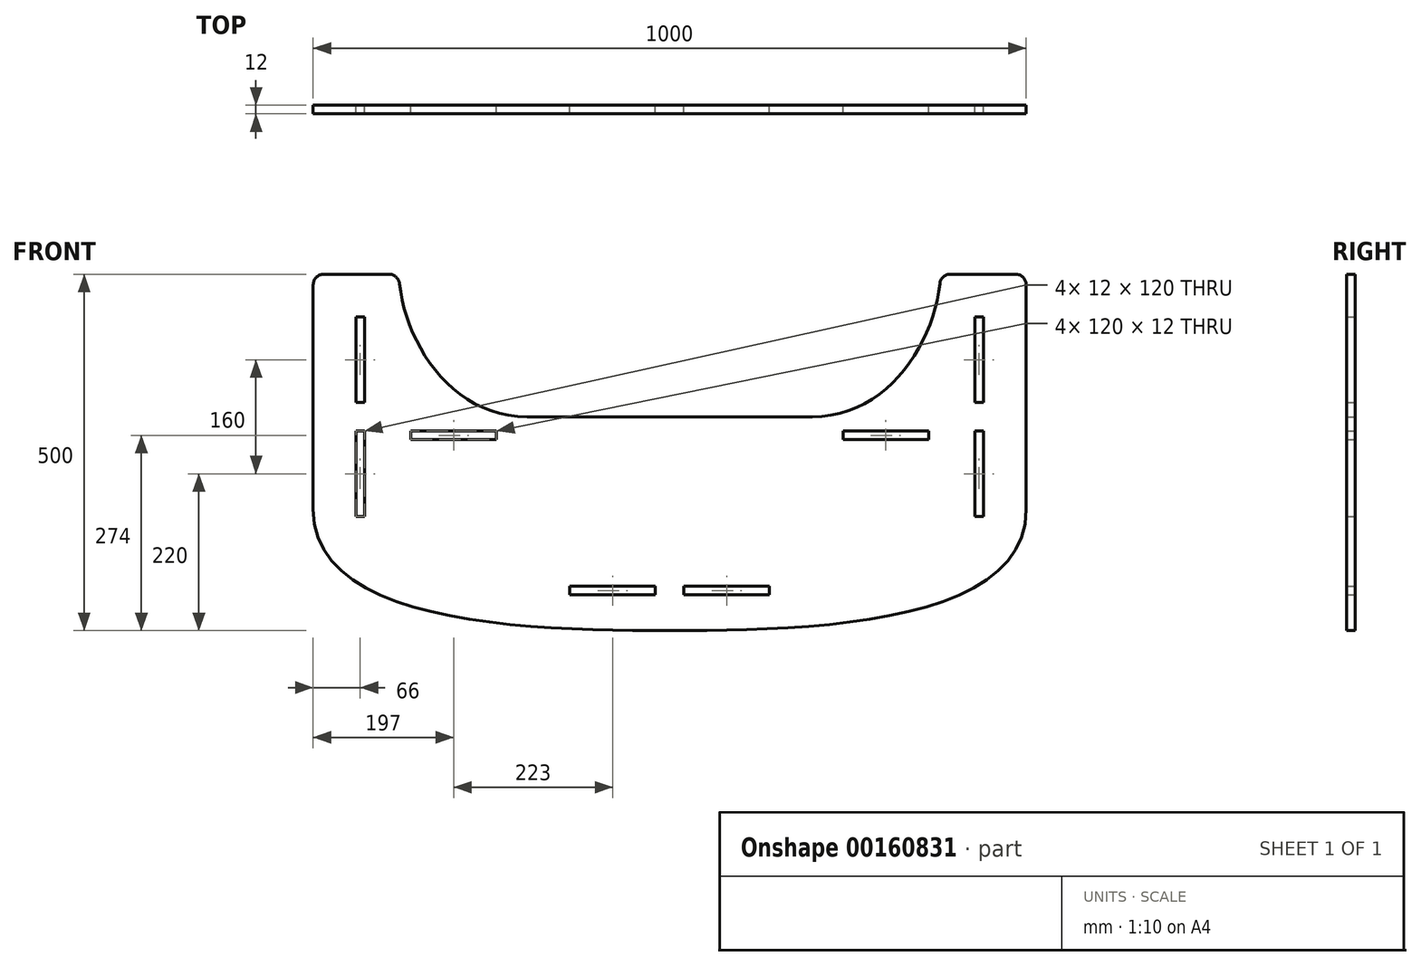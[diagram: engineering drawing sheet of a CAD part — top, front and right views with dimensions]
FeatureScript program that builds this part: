
annotation { "Feature Type Name" : "Feature", "Feature Type Description" : "" }
export const myFeature = defineFeature(function(context is Context, id is Id, definition is map)
    precondition{}
    {
        {
            var Q0;
            Q0=qCreatedBy(makeId("Front.planeOp"),FACE);
            var sketch = newSketch(context, id + "F0", { "sketchPlane" : qUnion([Q0])});
            skLineSegment(sketch, "E0", {"start": v(0, 0) * mm, "end": v(0, 300) * mm, "construction": true});
            skLineSegment(sketch, "E1", {"start": v(-393.84, 500) * mm, "end": v(-485, 500) * mm});
            skLineSegment(sketch, "E2", {"start": v(-500, 485) * mm, "end": v(-500, 170) * mm});
            skFitSpline(sketch, "E3", {"points": [v(-500, 170) * mm, v(0, 0) * mm], "startDerivative": vector(0, -492.34) * mm, "endDerivative": vector(572.83, 0) * mm});
            skLineSegment(sketch, "E4", {"start": v(-440, 440) * mm, "end": v(-440, 320) * mm});
            skLineSegment(sketch, "E5", {"start": v(-428, 320) * mm, "end": v(-428, 440) * mm});
            skLineSegment(sketch, "E6", {"start": v(-428, 440) * mm, "end": v(-440, 440) * mm});
            skLineSegment(sketch, "E7.bottom", {"start": v(-440, 280) * mm, "end": v(-428, 280) * mm});
            skLineSegment(sketch, "E7.top", {"start": v(-440, 160) * mm, "end": v(-428, 160) * mm});
            skLineSegment(sketch, "E7.left", {"start": v(-440, 280) * mm, "end": v(-440, 160) * mm});
            skLineSegment(sketch, "E7.right", {"start": v(-428, 280) * mm, "end": v(-428, 160) * mm});
            skLineSegment(sketch, "E8.bottom", {"start": v(-363, 280) * mm, "end": v(-243, 280) * mm});
            skLineSegment(sketch, "E8.top", {"start": v(-363, 268) * mm, "end": v(-243, 268) * mm});
            skLineSegment(sketch, "E8.left", {"start": v(-363, 280) * mm, "end": v(-363, 268) * mm});
            skLineSegment(sketch, "E8.right", {"start": v(-243, 280) * mm, "end": v(-243, 268) * mm});
            skLineSegment(sketch, "E9.bottom", {"start": v(-140, 62) * mm, "end": v(-20, 62) * mm});
            skLineSegment(sketch, "E9.top", {"start": v(-140, 50) * mm, "end": v(-20, 50) * mm});
            skLineSegment(sketch, "E9.left", {"start": v(-140, 62) * mm, "end": v(-140, 50) * mm});
            skLineSegment(sketch, "E9.right", {"start": v(-20, 62) * mm, "end": v(-20, 50) * mm});
            skLineSegment(sketch, "E10", {"start": v(-440, 320) * mm, "end": v(-428, 320) * mm});
            skLineSegment(sketch, "E11", {"start": v(0, 300) * mm, "end": v(-200, 300) * mm});
            skFitSpline(sketch, "E12", {"points": [v(-380, 500) * mm, v(-200, 300) * mm], "startDerivative": vector(12.74, -268.24) * mm, "endDerivative": vector(329.8, 0) * mm});
            skLineSegment(sketch, "E13.MirrorCS", {"start": v(440, 280) * mm, "end": v(428, 280) * mm});
            skLineSegment(sketch, "E14.MirrorCS", {"start": v(140, 62) * mm, "end": v(140, 50) * mm});
            skLineSegment(sketch, "E15.MirrorCS", {"start": v(440, 320) * mm, "end": v(428, 320) * mm});
            skLineSegment(sketch, "E16.MirrorCS", {"start": v(440, 160) * mm, "end": v(428, 160) * mm});
            skLineSegment(sketch, "E17.MirrorCS", {"start": v(428, 440) * mm, "end": v(440, 440) * mm});
            skLineSegment(sketch, "E18.MirrorCS", {"start": v(243, 280) * mm, "end": v(243, 268) * mm});
            skLineSegment(sketch, "E19.MirrorCS", {"start": v(363, 280) * mm, "end": v(363, 268) * mm});
            skLineSegment(sketch, "E20.MirrorCS", {"start": v(20, 62) * mm, "end": v(20, 50) * mm});
            skLineSegment(sketch, "E21.MirrorCS", {"start": v(363, 268) * mm, "end": v(243, 268) * mm});
            skLineSegment(sketch, "E22.MirrorCS", {"start": v(0, 300) * mm, "end": v(200, 300) * mm});
            skLineSegment(sketch, "E23.MirrorCS", {"start": v(363, 280) * mm, "end": v(243, 280) * mm});
            skLineSegment(sketch, "E24.MirrorCS", {"start": v(140, 50) * mm, "end": v(20, 50) * mm});
            skFitSpline(sketch, "E25.MirrorCS", {"points": [v(380, 500) * mm, v(200, 300) * mm], "startDerivative": vector(-12.74, -268.24) * mm, "endDerivative": vector(-329.8, 0) * mm});
            skLineSegment(sketch, "E26.MirrorCS", {"start": v(140, 62) * mm, "end": v(20, 62) * mm});
            skLineSegment(sketch, "E27.MirrorCS", {"start": v(428, 280) * mm, "end": v(428, 160) * mm});
            skLineSegment(sketch, "E28.MirrorCS", {"start": v(440, 280) * mm, "end": v(440, 160) * mm});
            skLineSegment(sketch, "E29.MirrorCS", {"start": v(428, 320) * mm, "end": v(428, 440) * mm});
            skLineSegment(sketch, "E30.MirrorCS", {"start": v(440, 440) * mm, "end": v(440, 320) * mm});
            skFitSpline(sketch, "E31.MirrorCS", {"points": [v(500, 170) * mm, v(0, 0) * mm], "startDerivative": vector(0, -492.34) * mm, "endDerivative": vector(-572.83, 0) * mm});
            skLineSegment(sketch, "E32.MirrorCS", {"start": v(500, 485) * mm, "end": v(500, 170) * mm});
            skLineSegment(sketch, "E33.MirrorCS", {"start": v(393.84, 500) * mm, "end": v(485, 500) * mm});
            skPoint(sketch, "E34.visualSharp", {"position": v(-500, 500) * mm});
            skArc(sketch, "E34.filletArc", {"start": v(-485, 500) * mm, "mid": v(-495.6, 495.6) * mm, "end": v(-500, 485) * mm});
            skArc(sketch, "E35.filletArc", {"start": v(393.84, 500) * mm, "mid": v(383.84, 496.18) * mm, "end": v(378.93, 486.68) * mm});
            skPoint(sketch, "E36.visualSharp", {"position": v(500, 500) * mm});
            skArc(sketch, "E36.filletArc", {"start": v(500, 485) * mm, "mid": v(495.6, 495.6) * mm, "end": v(485, 500) * mm});
            skArc(sketch, "E37.filletArc", {"start": v(-378.93, 486.68) * mm, "mid": v(-383.84, 496.18) * mm, "end": v(-393.84, 500) * mm});
            skSolve(sketch);
        }
        {
            var Q0;
            Q0=makeQuery(id+"F0.imprint","IMPRINT",FACE,{"disambiguationData":[TD([[makeQuery(id+"F0.imprint","IMPRINT",EDGE,{"derivedFrom":sQuery(id+"F0.wireOp",EDGE,"E1")}),1.0]])]});
            extrude(context, id + "F1", {"entities" : qUnion([Q0]), "depth" : 12 * mm});
        }
    });
